# Revit family: Toilet-Elongated-Right_Height-American_Standard-Colony-221AA_Series
name_source: partatom
category: Plumbing Fixtures
units: mm (PartAtom-declared; Revit-internal decimal feet)

## family parameters
Always vertical = No
Cut with Voids When Loaded = No
OmniClass Number = 23.45.05.21.11.11
OmniClass Title = Water Operated Water Closets
Part Type = Normal
Room Calculation Point = No
Round Connector Dimension = Use Radius
Shared = Yes
Work Plane-Based = Yes

## types (5) — shared parameters
ADA Compliant = Yes
ASME A112.18.1/CSA B125.1 = Yes
Assembly Code = D2010110
Bowl Shape = Elongated
CW Connection = Yes
CWFU = 10
Cold Water Connection Diameter = 3/8"
Cold Water Connection Height = 10"
Cold Water Connection Radius = 3/16"
Cold Water Connection Width = 6"
Default Elevation = 0"
Description = Colony Right Height Elongated 12 Inch Rough- In 1.6 gpf Toilet
Flush Rate = 1.6 gpf (6.0 Lpf)
HW Connection = No
Height = 30 7/8"
Installation Type = Floor Mounted
Length = 29 3/4"
Manufacturer = American Standard
Price = Prices may vary. Please consult Manufacturer Representative for most up-to-date price list.
Revised Date = 01/14/2019
URL = http://www.americanstandard-us.com
US EPA WaterSense Specification for HETs = Yes
Vent Connection = No
WFU = 10
Warranty Information = 2 Year Limited
Waste Connection = Yes
Waste Connection Diameter = 2"
Waste Connection Radius = 1"
Width = 19 3/16"
zero-valued in all types: HWFU

## per-type parameters (varying)
| type | Finish | Left Trip Lever | Locking Device | Material | Product Page URL | Right Trip Lever |
| 221AA.004.020 | Vitreous China-American Standard-020-White | Yes | No | Vitreous China-American Standard-020-White | https://www.americanstandard-us.com | No |
| 221AA.004.021 | Vitreous China-American Standard-021-Bone | Yes | No | Vitreous China-American Standard-021-Bone | https://www.americanstandard-us.com | No |
| 221AA.005.020 | Vitreous China-American Standard-020-White | No | No | Vitreous China-American Standard-020-White | https://www.americanstandard-us.com | Yes |
| 221AA.004.222 | Vitreous China-American Standard-222-Linen | Yes | No | Vitreous China-American Standard-222-Linen | https://www.americanstandard-us.com | No |
| 221AA.064.020 | Vitreous China-American Standard-020-White | Yes | Yes | Vitreous China-American Standard-020-White |  | No |

note: column(s) folded — value = type name in every type: Model

## geometry (parser evidence)
native form markers: Sweep x2
no freeform markers — native parametric forms only
